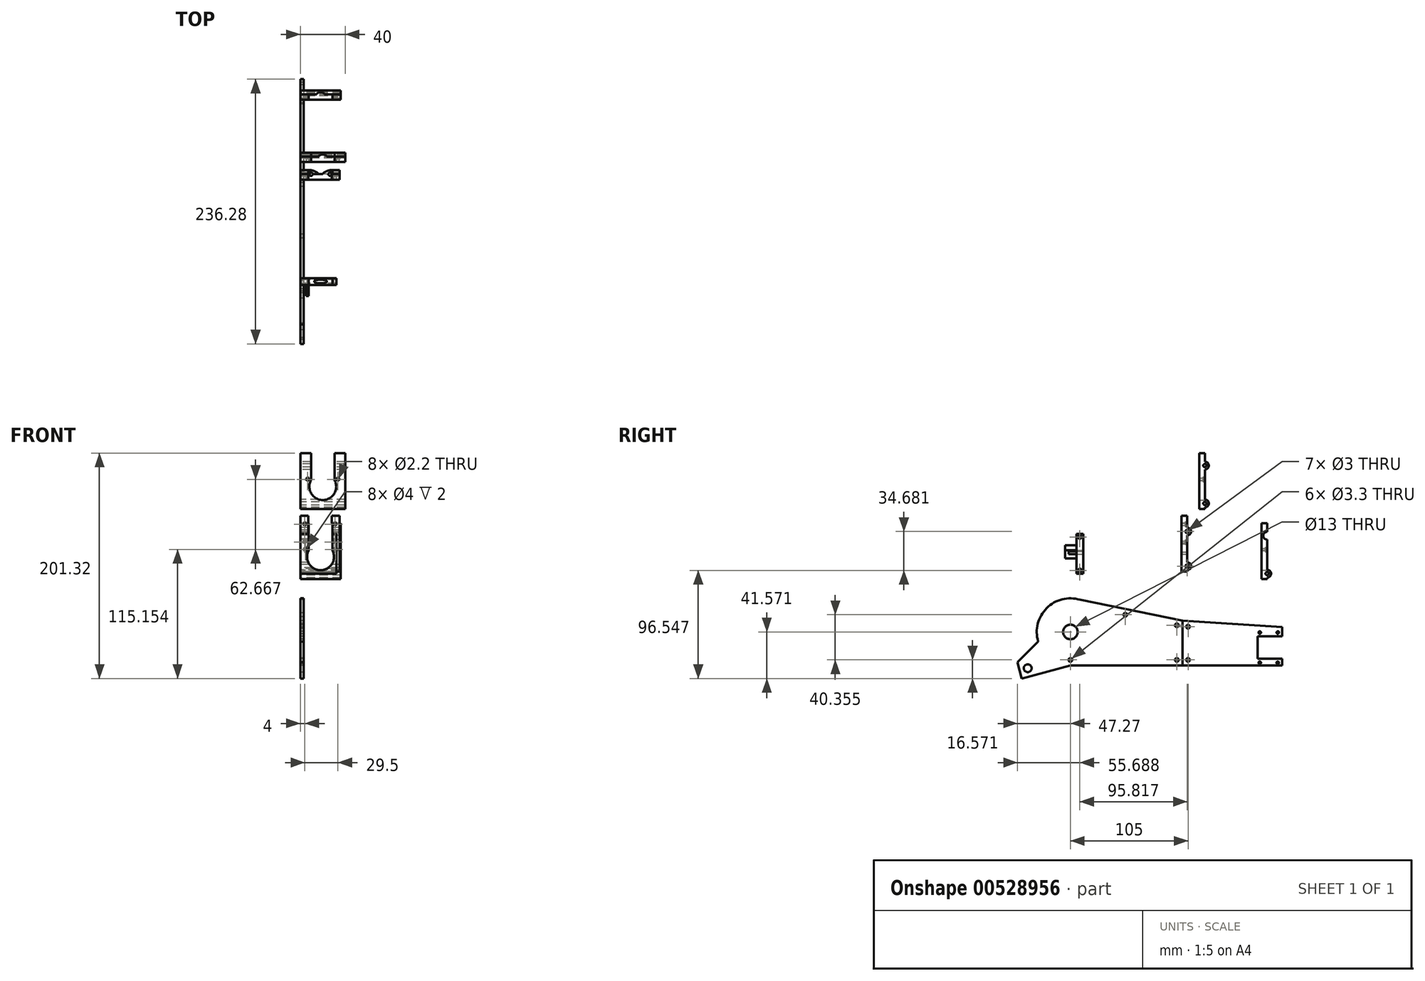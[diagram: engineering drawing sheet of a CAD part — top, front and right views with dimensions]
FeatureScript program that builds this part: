
annotation { "Feature Type Name" : "Feature", "Feature Type Description" : "" }
export const myFeature = defineFeature(function(context is Context, id is Id, definition is map)
    precondition{}
    {
        {
            var Q0;
            Q0=qCreatedBy(makeId("Right.planeOp"),FACE);
            var sketch = newSketch(context, id + "F0", { "sketchPlane" : qUnion([Q0])});
            skLineSegment(sketch, "E0", {"start": v(45.86, -61.42) * mm, "end": v(45.86, -101.42) * mm});
            skLineSegment(sketch, "E1", {"start": v(45.86, -101.42) * mm, "end": v(134.87, -101.42) * mm});
            skLineSegment(sketch, "E2", {"start": v(134.87, -101.42) * mm, "end": v(134.87, -95.42) * mm});
            skLineSegment(sketch, "E3", {"start": v(134.87, -66.9) * mm, "end": v(45.86, -61.42) * mm});
            skLineSegment(sketch, "E4", {"start": v(134.87, -95.42) * mm, "end": v(112.87, -95.42) * mm});
            skLineSegment(sketch, "E5", {"start": v(112.87, -95.42) * mm, "end": v(112.87, -75.42) * mm});
            skLineSegment(sketch, "E6", {"start": v(112.87, -75.42) * mm, "end": v(134.87, -75.42) * mm});
            skLineSegment(sketch, "E7.trimOffspring", {"start": v(134.87, -75.42) * mm, "end": v(134.87, -66.9) * mm});
            skPoint(sketch, "E8", {"position": v(50.86, -66.74) * mm});
            skPoint(sketch, "E9", {"position": v(50.86, -96.42) * mm});
            skCircle(sketch, "E10", {"center": v(145.37, -85.42) * mm, "radius": 11 * mm, "construction": true});
            skPoint(sketch, "E11", {"position": v(130.87, -98.92) * mm});
            skPoint(sketch, "E12", {"position": v(114.87, -98.92) * mm});
            skPoint(sketch, "E13", {"position": v(114.87, -71.92) * mm});
            skPoint(sketch, "E14", {"position": v(130.96, -71.92) * mm});
            skLineSegment(sketch, "E15", {"start": v(145.37, -85.42) * mm, "end": v(112.87, -85.42) * mm, "construction": true});
            skCircle(sketch, "E16", {"center": v(50.86, -66.74) * mm, "radius": 1.65 * mm});
            skCircle(sketch, "E17", {"center": v(50.86, -96.42) * mm, "radius": 1.65 * mm});
            skCircle(sketch, "E18", {"center": v(114.87, -71.92) * mm, "radius": 1.1 * mm});
            skCircle(sketch, "E19", {"center": v(130.96, -71.92) * mm, "radius": 1.1 * mm});
            skCircle(sketch, "E20", {"center": v(130.87, -98.92) * mm, "radius": 1.1 * mm});
            skCircle(sketch, "E21", {"center": v(114.87, -98.92) * mm, "radius": 1.1 * mm});
            skSolve(sketch);
        }
        {
            var Q0;
            Q0=makeQuery(id+"F0.imprint","IMPRINT",FACE,{"disambiguationData":[TD([[makeQuery(id+"F0.imprint","IMPRINT",EDGE,{"derivedFrom":sQuery(id+"F0.wireOp",EDGE,"E0")}),1.0]])]});
            extrude(context, id + "F1", {"entities" : qUnion([Q0]), "depth" : 3 * mm, "offsetDistance" : 25 * mm});
        }
        {
            var Q0;
            Q0=qCreatedBy(makeId("Right.planeOp"),FACE);
            var sketch = newSketch(context, id + "F2", { "sketchPlane" : qUnion([Q0])});
            skLineSegment(sketch, "E22", {"start": v(45.86, -61.42) * mm, "end": v(45.86, -101.42) * mm});
            skLineSegment(sketch, "E23", {"start": v(45.86, -101.42) * mm, "end": v(-54.14, -101.42) * mm});
            skArc(sketch, "E24", {"start": v(-54.14, -101.42) * mm, "mid": v(-83.82, -67.06) * mm, "end": v(-45.52, -42.68) * mm, "construction": true});
            skLineSegment(sketch, "E25", {"start": v(45.86, -61.42) * mm, "end": v(-45.52, -42.68) * mm});
            skCircle(sketch, "E26", {"center": v(-54.14, -71.42) * mm, "radius": 6.5 * mm});
            skLineSegment(sketch, "E27", {"start": v(-97.53, -113) * mm, "end": v(-101.41, -98.5) * mm});
            skLineSegment(sketch, "E28", {"start": v(-101.41, -98.5) * mm, "end": v(-82.9, -79.98) * mm});
            skCircle(sketch, "E29", {"center": v(-92.23, -103.81) * mm, "radius": 3.5 * mm});
            skLineSegment(sketch, "E30", {"start": v(-54.14, -71.42) * mm, "end": v(-92.23, -103.81) * mm, "construction": true});
            skLineSegment(sketch, "E31", {"start": v(-97.53, -113) * mm, "end": v(-54.14, -101.42) * mm});
            skPoint(sketch, "E32", {"position": v(40.86, -65.5) * mm});
            skPoint(sketch, "E33", {"position": v(40.86, -96.42) * mm});
            skLineSegment(sketch, "E34", {"start": v(-54.14, -71.42) * mm, "end": v(-54.14, -101.42) * mm, "construction": true});
            skPoint(sketch, "E35", {"position": v(-54.14, -96.42) * mm});
            skLineSegment(sketch, "E36", {"start": v(-54.14, -71.42) * mm, "end": v(-15.15, -48.9) * mm, "construction": true});
            skPoint(sketch, "E37", {"position": v(-5.15, -56.06) * mm});
            skCircle(sketch, "E38", {"center": v(-5.15, -56.06) * mm, "radius": 1.65 * mm});
            skCircle(sketch, "E39", {"center": v(40.86, -65.5) * mm, "radius": 1.65 * mm});
            skCircle(sketch, "E40", {"center": v(40.86, -96.42) * mm, "radius": 1.65 * mm});
            skCircle(sketch, "E41", {"center": v(-54.14, -96.42) * mm, "radius": 1.65 * mm});
            skArc(sketch, "E42", {"start": v(-45.52, -42.68) * mm, "mid": v(-75.33, -50.19) * mm, "end": v(-82.9, -79.98) * mm});
            skSolve(sketch);
        }
        {
            var Q0;
            {var subQ7=sQuery(id+"F2.wireOp",EDGE,"E22");Q0=makeQuery(id+"F2.imprint","IMPRINT",FACE,{"disambiguationData":[TD([[makeQuery(id+"F2.imprint","IMPRINT",EDGE,{"derivedFrom":subQ7}),-1.0]])]});}
            var Q1;
            {var subQ6=sQuery(id+"F2.wireOp",EDGE,"E24");var subQ9=makeQuery(id+"F2.imprint","INTERSECT",VERTEX,{"derivedFrom":[subQ6,sQuery(id+"F2.wireOp",EDGE,"E28")]});Q1=makeQuery(id+"F2.imprint","IMPRINT",FACE,{"disambiguationData":[TD([[makeQuery(id+"F2.imprint","IMPRINT",EDGE,{"disambiguationData":[TD([[subQ9,1.0]])],"derivedFrom":subQ6}),-1.0]])]});}
            var Q2;
            Q2=makeQuery(id+"F2.imprint","IMPRINT",FACE,{"disambiguationData":[TD([[makeQuery(id+"F2.imprint","IMPRINT",EDGE,{"derivedFrom":sQuery(id+"F2.wireOp",EDGE,"E27")}),-1.0]])]});
            extrude(context, id + "F3", {"entities" : qUnion([Q0, Q1, Q2]), "depth" : 3 * mm, "offsetDistance" : 25 * mm});
        }
        {
            var Q0;
            Q0=qCreatedBy(makeId("Right.planeOp"),FACE);
            var sketch = newSketch(context, id + "F4", { "sketchPlane" : qUnion([Q0])});
            skLineSegment(sketch, "E43", {"start": v(50.1, 32.32) * mm, "end": v(50.1, -17.68) * mm});
            skLineSegment(sketch, "E44", {"start": v(50.1, -17.68) * mm, "end": v(45.1, -17.68) * mm});
            skLineSegment(sketch, "E45", {"start": v(45.1, -17.68) * mm, "end": v(45.1, 32.32) * mm});
            skLineSegment(sketch, "E46", {"start": v(45.1, 32.32) * mm, "end": v(50.1, 32.32) * mm});
            skCircle(sketch, "E47", {"center": v(50.1, -12.68) * mm, "radius": 1.5 * mm});
            skCircle(sketch, "E48", {"center": v(50.1, -12.68) * mm, "radius": 3.5 * mm});
            skCircle(sketch, "E49", {"center": v(50.1, 18.24) * mm, "radius": 1.5 * mm});
            skCircle(sketch, "E50", {"center": v(50.1, 18.24) * mm, "radius": 3.5 * mm});
            skSolve(sketch);
        }
        {
            var Q0;
            Q0 = qSketchRegion(id + "F4", true);
            extrude(context, id + "F5", {"entities" : qUnion([Q0]), "depth" : 35 * mm, "offsetDistance" : 25 * mm});
        }
        {
            var Q0;
            {var subQ0=sQuery(id+"F4.wireOp",EDGE,"E43");Q0=makeQuery(id+"F5.opExtrude","SWEPT_FACE",FACE,{"disambiguationData":[OSD([subQ0]),TDD([makeQuery(id+"F4.imprint","IMPRINT",EDGE,{"disambiguationData":[TD([[makeQuery(id+"F4.imprint","INTERSECT",VERTEX,{"derivedFrom":[subQ0,sQuery(id+"F4.wireOp",EDGE,"E46")]}),-1.0]])],"derivedFrom":subQ0})])]});}
            var sketch = newSketch(context, id + "F6", { "sketchPlane" : qUnion([Q0])});
            skCircle(sketch, "E51", {"center": v(-17.5, 2.32) * mm, "radius": 12 * mm});
            skPoint(sketch, "E52", {"position": v(-4, 24.82) * mm});
            skPoint(sketch, "E53", {"position": v(-4, 8.82) * mm});
            skPoint(sketch, "E54", {"position": v(-31, 8.82) * mm});
            skPoint(sketch, "E55", {"position": v(-31, 24.82) * mm});
            skLineSegment(sketch, "E56", {"start": v(-7, 8.13) * mm, "end": v(-7, 32.32) * mm});
            skLineSegment(sketch, "E57", {"start": v(-28, 32.32) * mm, "end": v(-28, 8.13) * mm});
            skSolve(sketch);
        }
        {
            var Q0;
            Q0=sQuery(id+"F6.wireOp",VERTEX,"E52");
            var Q1;
            Q1=sQuery(id+"F6.wireOp",VERTEX,"E53");
            var Q2;
            Q2=sQuery(id+"F6.wireOp",VERTEX,"E55");
            var Q3;
            Q3=sQuery(id+"F6.wireOp",VERTEX,"E54");
            var Q4;
            Q4=makeQuery(id+"FsGmeQWHbg3FPz0_0.opExtrude","SWEPT_BODY",BODY,{"disambiguationData":[OSD([sQuery(id+"FrUOqRR2quuCKey_0.wireOp",EDGE,"gyZbDc0t-850H-gwzf-YuIU-PHWtBzP6e17o.bottom"),sQuery(id+"FrUOqRR2quuCKey_0.wireOp",EDGE,"gyZbDc0t-850H-gwzf-YuIU-PHWtBzP6e17o.top"),sQuery(id+"FrUOqRR2quuCKey_0.wireOp",EDGE,"gyZbDc0t-850H-gwzf-YuIU-PHWtBzP6e17o.left"),sQuery(id+"FrUOqRR2quuCKey_0.wireOp",EDGE,"gyZbDc0t-850H-gwzf-YuIU-PHWtBzP6e17o.right")])]});
            var Q5;
            Q5=makeQuery(id+"F5.opExtrude","SWEPT_BODY",BODY,{"disambiguationData":[OSD([sQuery(id+"F4.wireOp",EDGE,"E43"),sQuery(id+"F4.wireOp",EDGE,"E44"),sQuery(id+"F4.wireOp",EDGE,"E45"),sQuery(id+"F4.wireOp",EDGE,"E46"),sQuery(id+"F4.wireOp",EDGE,"E47"),sQuery(id+"F4.wireOp",EDGE,"E48"),sQuery(id+"F4.wireOp",EDGE,"E49"),sQuery(id+"F4.wireOp",EDGE,"E50")])]});
            hole(context, id + "F7", {"style" : HoleStyle.C_BORE, "endStyle" : HoleEndStyle.BLIND, "holeDiameter" : 2.2 * mm, "cBoreDiameter" : 4 * mm, "cBoreDepth" : 2 * mm, "holeDepth" : 12 * mm, "isTappedThrough" : true, "tappedDepth" : 12 * mm, "tapClearance" : 3, "locations" : qUnion([Q0, Q1, Q2, Q3]), "scope" : qUnion([Q4, Q5])});
        }
        {
            var Q0;
            Q0 = qSketchRegion(id + "F6", true);
            var Q1;
            {var subQ0=sQuery(id+"F6.wireOp",EDGE,"E56");var subQ1=sQuery(id+"F6.wireOp",EDGE,"E51");var subQ2=makeQuery(id+"F6.imprint","INTERSECT",VERTEX,{"derivedFrom":[subQ1,subQ0]});Q1=makeQuery(id+"F6.imprint","IMPRINT",FACE,{"disambiguationData":[TD([[makeQuery(id+"F6.imprint","IMPRINT",EDGE,{"disambiguationData":[TD([[subQ2,-1.0]])],"derivedFrom":subQ1}),-1.0]])]});}
            var Q2;
            {var subQ0=sQuery(id+"F6.wireOp",EDGE,"E56");var subQ1=sQuery(id+"F4.wireOp",EDGE,"E43");var subQ2=makeQuery(id+"F5.opExtrude","SWEPT_EDGE",EDGE,{"disambiguationData":[OSD([subQ1,sQuery(id+"F4.wireOp",EDGE,"E46")])]});var subQ3=makeQuery(id+"F6.imprint","INTERSECT",VERTEX,{"derivedFrom":[subQ2,subQ0]});Q2=makeQuery(id+"F6.imprint","IMPRINT",FACE,{"disambiguationData":[TD([[makeQuery(id+"F6.imprint","IMPRINT",EDGE,{"disambiguationData":[TD([[subQ3,1.0]])],"derivedFrom":subQ0}),1.0]])]});}
            extrude(context, id + "F8", {"entities" : qUnion([Q0, Q1, Q2]), "operationType" : NewBodyOperationType.REMOVE, "oppositeDirection" : true, "depth" : 25 * mm, "offsetDistance" : 25 * mm, "hasSecondDirection" : true, "secondDirectionOppositeDirection" : false, "secondDirectionDepth" : 25 * mm});
        }
        {
            var Q0;
            Q0=qCreatedBy(makeId("Right.planeOp"),FACE);
            var sketch = newSketch(context, id + "F9", { "sketchPlane" : qUnion([Q0])});
            skLineSegment(sketch, "E58.bottom", {"start": v(-48.72, 16.24) * mm, "end": v(-42.72, 16.24) * mm});
            skLineSegment(sketch, "E58.top", {"start": v(-48.72, -19.3) * mm, "end": v(-42.72, -19.3) * mm});
            skLineSegment(sketch, "E58.left", {"start": v(-48.72, 16.24) * mm, "end": v(-48.72, -19.3) * mm});
            skLineSegment(sketch, "E58.right", {"start": v(-42.72, 16.24) * mm, "end": v(-42.72, -19.3) * mm});
            skPoint(sketch, "E59", {"position": v(-45.72, 13.24) * mm});
            skPoint(sketch, "E60", {"position": v(-45.72, -16.44) * mm});
            skSolve(sketch);
        }
        {
            var Q0;
            Q0 = qSketchRegion(id + "F9", true);
            extrude(context, id + "F10", {"entities" : qUnion([Q0]), "depth" : 32 * mm, "offsetDistance" : 25 * mm});
        }
        {
            var Q0;
            Q0=sQuery(id+"F9.wireOp",VERTEX,"E59");
            var Q1;
            Q1=sQuery(id+"F9.wireOp",VERTEX,"E60");
            var Q2;
            Q2=makeQuery(id+"F10.opExtrude","SWEPT_BODY",BODY,{"disambiguationData":[OSD([sQuery(id+"F9.wireOp",EDGE,"E58.bottom"),sQuery(id+"F9.wireOp",EDGE,"E58.top"),sQuery(id+"F9.wireOp",EDGE,"E58.left"),sQuery(id+"F9.wireOp",EDGE,"E58.right")])]});
            hole(context, id + "F11", {"style" : HoleStyle.SIMPLE, "endStyle" : HoleEndStyle.THROUGH, "oppositeDirection" : true, "holeDiameter" : 3 * mm, "majorDiameter" : 5 * mm, "isTappedThrough" : true, "tappedDepth" : 12 * mm, "tapClearance" : 3, "locations" : qUnion([Q0, Q1]), "scope" : qUnion([Q2])});
        }
        {
            var Q0;
            Q0=makeQuery(id+"F10.opExtrude","SWEPT_FACE",FACE,{"disambiguationData":[OSD([sQuery(id+"F9.wireOp",EDGE,"E58.right")])]});
            var sketch = newSketch(context, id + "F12", { "sketchPlane" : qUnion([Q0])});
            skCircle(sketch, "E61", {"center": v(-16, -1.1) * mm, "radius": 8 * mm, "construction": true});
            skLineSegment(sketch, "E62", {"start": v(-16, 6.9) * mm, "end": v(-16, -9.1) * mm, "construction": true});
            skLineSegment(sketch, "E63", {"start": v(-8, -1.1) * mm, "end": v(-24, -1.1) * mm, "construction": true});
            skPoint(sketch, "E64", {"position": v(-24, -1.1) * mm});
            skPoint(sketch, "E65", {"position": v(-16, 6.9) * mm});
            skPoint(sketch, "E66", {"position": v(-8, -1.1) * mm});
            skPoint(sketch, "E67", {"position": v(-16, -9.1) * mm});
            skCircle(sketch, "E68", {"center": v(-16, -1.1) * mm, "radius": 11 * mm});
            skSolve(sketch);
        }
        {
            var Q0;
            Q0 = qSketchRegion(id + "F12", true);
            extrude(context, id + "F13", {"entities" : qUnion([Q0]), "operationType" : NewBodyOperationType.ADD, "oppositeDirection" : true, "depth" : 16 * mm, "offsetDistance" : 25 * mm});
        }
        {
            var Q0;
            Q0=sQuery(id+"F12.wireOp",VERTEX,"E65");
            var Q1;
            Q1=sQuery(id+"F12.wireOp",VERTEX,"E66");
            var Q2;
            Q2=sQuery(id+"F12.wireOp",VERTEX,"E67");
            var Q3;
            Q3=sQuery(id+"F12.wireOp",VERTEX,"E64");
            var Q4;
            Q4=makeQuery(id+"F10.opExtrude","SWEPT_BODY",BODY,{"disambiguationData":[OSD([sQuery(id+"F9.wireOp",EDGE,"E58.bottom"),sQuery(id+"F9.wireOp",EDGE,"E58.top"),sQuery(id+"F9.wireOp",EDGE,"E58.left"),sQuery(id+"F9.wireOp",EDGE,"E58.right")])]});
            hole(context, id + "F14", {"style" : HoleStyle.C_BORE, "endStyle" : HoleEndStyle.THROUGH, "holeDiameter" : 2.2 * mm, "cBoreDiameter" : 4 * mm, "cBoreDepth" : 13 * mm, "majorDiameter" : 5 * mm, "isTappedThrough" : true, "tappedDepth" : 12 * mm, "tapClearance" : 3, "locations" : qUnion([Q0, Q1, Q2, Q3]), "scope" : qUnion([Q4])});
        }
        {
            var Q0;
            Q0=qCreatedBy(makeId("Right.planeOp"),FACE);
            var sketch = newSketch(context, id + "F15", { "sketchPlane" : qUnion([Q0])});
            skLineSegment(sketch, "E69", {"start": v(121.46, 25.66) * mm, "end": v(121.46, -24.34) * mm});
            skLineSegment(sketch, "E70", {"start": v(121.46, -24.34) * mm, "end": v(116.46, -24.34) * mm});
            skLineSegment(sketch, "E71", {"start": v(116.46, -24.34) * mm, "end": v(116.46, 25.66) * mm});
            skLineSegment(sketch, "E72", {"start": v(116.46, 25.66) * mm, "end": v(121.46, 25.66) * mm});
            skCircle(sketch, "E73", {"center": v(121.46, -19.34) * mm, "radius": 1.45 * mm});
            skCircle(sketch, "E74", {"center": v(121.46, -19.34) * mm, "radius": 3.5 * mm});
            skCircle(sketch, "E75", {"center": v(121.46, 14.46) * mm, "radius": 1.45 * mm});
            skCircle(sketch, "E76", {"center": v(121.46, 14.46) * mm, "radius": 3.5 * mm});
            skSolve(sketch);
        }
        {
            var Q0;
            {var subQ0=sQuery(id+"F15.wireOp",EDGE,"E70");Q0=makeQuery(id+"F15.imprint","IMPRINT",FACE,{"disambiguationData":[TD([[makeQuery(id+"F15.imprint","IMPRINT",EDGE,{"derivedFrom":subQ0}),-1.0]])]});}
            var Q1;
            {var subQ0=sQuery(id+"F15.wireOp",EDGE,"E76");var subQ1=sQuery(id+"F15.wireOp",EDGE,"E69");var subQ2=makeQuery(id+"F15.imprint","INTERSECT",VERTEX,{"disambiguationData":[OD(0.0)],"derivedFrom":[subQ1,subQ0]});Q1=makeQuery(id+"F15.imprint","IMPRINT",FACE,{"disambiguationData":[TD([[makeQuery(id+"F15.imprint","IMPRINT",EDGE,{"disambiguationData":[TD([[subQ2,-1.0]])],"derivedFrom":subQ1}),1.0]])]});}
            var Q2;
            {var subQ0=sQuery(id+"F15.wireOp",EDGE,"E76");var subQ1=sQuery(id+"F15.wireOp",EDGE,"E69");var subQ2=makeQuery(id+"F15.imprint","INTERSECT",VERTEX,{"disambiguationData":[OD(0.0)],"derivedFrom":[subQ1,subQ0]});Q2=makeQuery(id+"F15.imprint","IMPRINT",FACE,{"disambiguationData":[TD([[makeQuery(id+"F15.imprint","IMPRINT",EDGE,{"disambiguationData":[TD([[subQ2,-1.0]])],"derivedFrom":subQ1}),-1.0]])]});}
            var Q3;
            {var subQ0=sQuery(id+"F15.wireOp",EDGE,"E74");var subQ1=sQuery(id+"F15.wireOp",EDGE,"E69");var subQ2=makeQuery(id+"F15.imprint","INTERSECT",VERTEX,{"disambiguationData":[OD(0.0)],"derivedFrom":[subQ1,subQ0]});Q3=makeQuery(id+"F15.imprint","IMPRINT",FACE,{"disambiguationData":[TD([[makeQuery(id+"F15.imprint","IMPRINT",EDGE,{"disambiguationData":[TD([[subQ2,-1.0]])],"derivedFrom":subQ1}),1.0]])]});}
            var Q4;
            {var subQ0=sQuery(id+"F15.wireOp",EDGE,"E74");var subQ1=sQuery(id+"F15.wireOp",EDGE,"E69");var subQ2=makeQuery(id+"F15.imprint","INTERSECT",VERTEX,{"disambiguationData":[OD(0.0)],"derivedFrom":[subQ1,subQ0]});Q4=makeQuery(id+"F15.imprint","IMPRINT",FACE,{"disambiguationData":[TD([[makeQuery(id+"F15.imprint","IMPRINT",EDGE,{"disambiguationData":[TD([[subQ2,-1.0]])],"derivedFrom":subQ1}),-1.0]])]});}
            extrude(context, id + "F16", {"entities" : qUnion([Q0, Q1, Q2, Q3, Q4]), "depth" : 36 * mm, "offsetDistance" : 25 * mm});
        }
        {
            var Q0;
            {var subQ0=sQuery(id+"F15.wireOp",EDGE,"E69");Q0=makeQuery(id+"F16.opExtrude","SWEPT_FACE",FACE,{"disambiguationData":[OSD([subQ0]),TDD([makeQuery(id+"F15.imprint","IMPRINT",EDGE,{"disambiguationData":[TD([[makeQuery(id+"F15.imprint","INTERSECT",VERTEX,{"derivedFrom":[subQ0,sQuery(id+"F15.wireOp",EDGE,"E72")]}),-1.0]])],"derivedFrom":subQ0})])]});}
            var sketch = newSketch(context, id + "F17", { "sketchPlane" : qUnion([Q0])});
            skCircle(sketch, "E77", {"center": v(-18, -4.34) * mm, "radius": 12 * mm});
            skPoint(sketch, "E78", {"position": v(-4.5, 18.16) * mm});
            skPoint(sketch, "E79", {"position": v(-31.5, 18.16) * mm});
            skPoint(sketch, "E80", {"position": v(-31.5, 2.16) * mm});
            skPoint(sketch, "E81", {"position": v(-4.5, 2.16) * mm});
            skLineSegment(sketch, "E82", {"start": v(-28.5, 1.47) * mm, "end": v(-28.5, 25.66) * mm});
            skLineSegment(sketch, "E83", {"start": v(-7.5, 1.47) * mm, "end": v(-7.5, 25.66) * mm});
            skSolve(sketch);
        }
        {
            var Q0;
            {var subQ0=sQuery(id+"F17.wireOp",EDGE,"E77");var subQ1=makeQuery(id+"F17.imprint","INTERSECT",VERTEX,{"derivedFrom":[subQ0,sQuery(id+"F17.wireOp",EDGE,"E82")]});Q0=makeQuery(id+"F17.imprint","IMPRINT",FACE,{"disambiguationData":[TD([[makeQuery(id+"F17.imprint","IMPRINT",EDGE,{"disambiguationData":[TD([[subQ1,1.0]])],"derivedFrom":subQ0}),1.0]])]});}
            var Q1;
            {var subQ0=sQuery(id+"F17.wireOp",EDGE,"E82");var subQ1=sQuery(id+"F15.wireOp",EDGE,"E69");var subQ2=makeQuery(id+"F16.opExtrude","SWEPT_EDGE",EDGE,{"disambiguationData":[OSD([subQ1,sQuery(id+"F15.wireOp",EDGE,"E72")])]});var subQ3=makeQuery(id+"F17.imprint","INTERSECT",VERTEX,{"derivedFrom":[subQ2,subQ0]});Q1=makeQuery(id+"F17.imprint","IMPRINT",FACE,{"disambiguationData":[TD([[makeQuery(id+"F17.imprint","IMPRINT",EDGE,{"disambiguationData":[TD([[subQ3,1.0]])],"derivedFrom":subQ0}),-1.0]])]});}
            var Q2;
            {var subQ0=sQuery(id+"F17.wireOp",EDGE,"E82");var subQ1=sQuery(id+"F17.wireOp",EDGE,"E77");var subQ2=makeQuery(id+"F17.imprint","INTERSECT",VERTEX,{"derivedFrom":[subQ1,subQ0]});Q2=makeQuery(id+"F17.imprint","IMPRINT",FACE,{"disambiguationData":[TD([[makeQuery(id+"F17.imprint","IMPRINT",EDGE,{"disambiguationData":[TD([[subQ2,1.0]])],"derivedFrom":subQ1}),-1.0]])]});}
            extrude(context, id + "F18", {"entities" : qUnion([Q0, Q1, Q2]), "operationType" : NewBodyOperationType.REMOVE, "endBound" : BoundingType.THROUGH_ALL, "oppositeDirection" : true, "depth" : 25 * mm, "offsetDistance" : 25 * mm, "hasSecondDirection" : true, "secondDirectionOppositeDirection" : false, "secondDirectionDepth" : 25 * mm});
        }
        {
            var Q0;
            Q0=sQuery(id+"F17.wireOp",VERTEX,"E80");
            var Q1;
            Q1=sQuery(id+"F17.wireOp",VERTEX,"E81");
            var Q2;
            Q2=makeQuery(id+"F16.opExtrude","SWEPT_BODY",BODY,{"disambiguationData":[OSD([sQuery(id+"F15.wireOp",EDGE,"E69"),sQuery(id+"F15.wireOp",EDGE,"E70"),sQuery(id+"F15.wireOp",EDGE,"E71"),sQuery(id+"F15.wireOp",EDGE,"E72"),sQuery(id+"F15.wireOp",EDGE,"E73"),sQuery(id+"F15.wireOp",EDGE,"E74"),sQuery(id+"F15.wireOp",EDGE,"E75"),sQuery(id+"F15.wireOp",EDGE,"E76")])]});
            hole(context, id + "F19", {"style" : HoleStyle.C_BORE, "endStyle" : HoleEndStyle.BLIND, "holeDiameter" : 2.2 * mm, "cBoreDiameter" : 4 * mm, "cBoreDepth" : 2 * mm, "majorDiameter" : 5 * mm, "holeDepth" : 12 * mm, "isTappedThrough" : true, "tappedDepth" : 12 * mm, "tapClearance" : 3, "locations" : qUnion([Q0, Q1]), "scope" : qUnion([Q2])});
        }
        {
            var Q0;
            Q0=qCreatedBy(makeId("Right.planeOp"),FACE);
            var sketch = newSketch(context, id + "F20", { "sketchPlane" : qUnion([Q0])});
            skLineSegment(sketch, "E84", {"start": v(65.88, 88.33) * mm, "end": v(65.88, 38.33) * mm});
            skLineSegment(sketch, "E85", {"start": v(65.88, 38.33) * mm, "end": v(60.88, 38.33) * mm});
            skLineSegment(sketch, "E86", {"start": v(60.88, 38.33) * mm, "end": v(60.88, 88.33) * mm});
            skLineSegment(sketch, "E87", {"start": v(60.88, 88.33) * mm, "end": v(65.88, 88.33) * mm});
            skCircle(sketch, "E88", {"center": v(65.88, 43.33) * mm, "radius": 1.45 * mm});
            skCircle(sketch, "E89", {"center": v(65.88, 43.33) * mm, "radius": 3.5 * mm});
            skCircle(sketch, "E90", {"center": v(65.88, 77.13) * mm, "radius": 1.45 * mm});
            skCircle(sketch, "E91", {"center": v(65.88, 77.13) * mm, "radius": 3.5 * mm});
            skSolve(sketch);
        }
        {
            var Q0;
            Q0 = qSketchRegion(id + "F20", true);
            extrude(context, id + "F21", {"entities" : qUnion([Q0]), "depth" : 40 * mm, "offsetDistance" : 25 * mm});
        }
        {
            var Q0;
            {var subQ0=sQuery(id+"F20.wireOp",EDGE,"E84");Q0=makeQuery(id+"F21.opExtrude","SWEPT_FACE",FACE,{"disambiguationData":[OSD([subQ0]),TDD([makeQuery(id+"F20.imprint","IMPRINT",EDGE,{"disambiguationData":[TD([[makeQuery(id+"F20.imprint","INTERSECT",VERTEX,{"derivedFrom":[subQ0,sQuery(id+"F20.wireOp",EDGE,"E87")]}),-1.0]])],"derivedFrom":subQ0})])]});}
            var sketch = newSketch(context, id + "F22", { "sketchPlane" : qUnion([Q0])});
            skLineSegment(sketch, "E92", {"start": v(-20, 80.63) * mm, "end": v(-20, 61.1) * mm, "construction": true});
            skCircle(sketch, "E93", {"center": v(-20, 58.33) * mm, "radius": 12 * mm});
            skPoint(sketch, "E94", {"position": v(-33.5, 80.83) * mm});
            skPoint(sketch, "E95", {"position": v(-6.5, 80.83) * mm});
            skPoint(sketch, "E96", {"position": v(-33.5, 64.83) * mm});
            skPoint(sketch, "E97", {"position": v(-6.5, 64.83) * mm});
            skLineSegment(sketch, "E98", {"start": v(-9.5, 88.33) * mm, "end": v(-9.5, 64.14) * mm});
            skLineSegment(sketch, "E99", {"start": v(-30.5, 88.33) * mm, "end": v(-30.5, 64.14) * mm});
            skSolve(sketch);
        }
        {
            var Q0;
            {var subQ0=sQuery(id+"F22.wireOp",EDGE,"E98");var subQ1=sQuery(id+"F20.wireOp",EDGE,"E84");var subQ2=makeQuery(id+"F21.opExtrude","SWEPT_EDGE",EDGE,{"disambiguationData":[OSD([subQ1,sQuery(id+"F20.wireOp",EDGE,"E87")])]});var subQ3=makeQuery(id+"F22.imprint","INTERSECT",VERTEX,{"derivedFrom":[subQ2,subQ0]});Q0=makeQuery(id+"F22.imprint","IMPRINT",FACE,{"disambiguationData":[TD([[makeQuery(id+"F22.imprint","IMPRINT",EDGE,{"disambiguationData":[TD([[subQ3,-1.0]])],"derivedFrom":subQ0}),-1.0]])]});}
            var Q1;
            {var subQ0=sQuery(id+"F22.wireOp",EDGE,"E93");var subQ1=makeQuery(id+"F22.imprint","INTERSECT",VERTEX,{"derivedFrom":[subQ0,sQuery(id+"F22.wireOp",EDGE,"E98")]});Q1=makeQuery(id+"F22.imprint","IMPRINT",FACE,{"disambiguationData":[TD([[makeQuery(id+"F22.imprint","IMPRINT",EDGE,{"disambiguationData":[TD([[subQ1,-1.0]])],"derivedFrom":subQ0}),1.0]])]});}
            var Q2;
            {var subQ0=sQuery(id+"F22.wireOp",EDGE,"E98");var subQ1=sQuery(id+"F22.wireOp",EDGE,"E93");var subQ2=makeQuery(id+"F22.imprint","INTERSECT",VERTEX,{"derivedFrom":[subQ1,subQ0]});Q2=makeQuery(id+"F22.imprint","IMPRINT",FACE,{"disambiguationData":[TD([[makeQuery(id+"F22.imprint","IMPRINT",EDGE,{"disambiguationData":[TD([[subQ2,-1.0]])],"derivedFrom":subQ1}),-1.0]])]});}
            extrude(context, id + "F23", {"entities" : qUnion([Q0, Q1, Q2]), "operationType" : NewBodyOperationType.REMOVE, "endBound" : BoundingType.SYMMETRIC, "oppositeDirection" : true, "depth" : 25 * mm, "offsetDistance" : 25 * mm});
        }
        {
            var Q0;
            Q0=sQuery(id+"F22.wireOp",VERTEX,"E96");
            var Q1;
            Q1=sQuery(id+"F22.wireOp",VERTEX,"E97");
            var Q2;
            Q2=makeQuery(id+"F21.opExtrude","SWEPT_BODY",BODY,{"disambiguationData":[OSD([sQuery(id+"F20.wireOp",EDGE,"E84"),sQuery(id+"F20.wireOp",EDGE,"E85"),sQuery(id+"F20.wireOp",EDGE,"E86"),sQuery(id+"F20.wireOp",EDGE,"E87"),sQuery(id+"F20.wireOp",EDGE,"E88"),sQuery(id+"F20.wireOp",EDGE,"E89"),sQuery(id+"F20.wireOp",EDGE,"E90"),sQuery(id+"F20.wireOp",EDGE,"E91")])]});
            hole(context, id + "F24", {"style" : HoleStyle.C_BORE, "endStyle" : HoleEndStyle.THROUGH, "holeDiameter" : 2.2 * mm, "cBoreDiameter" : 4 * mm, "cBoreDepth" : 2 * mm, "majorDiameter" : 5 * mm, "isTappedThrough" : true, "tappedDepth" : 12 * mm, "tapClearance" : 3, "locations" : qUnion([Q0, Q1]), "scope" : qUnion([Q2])});
        }
    });
